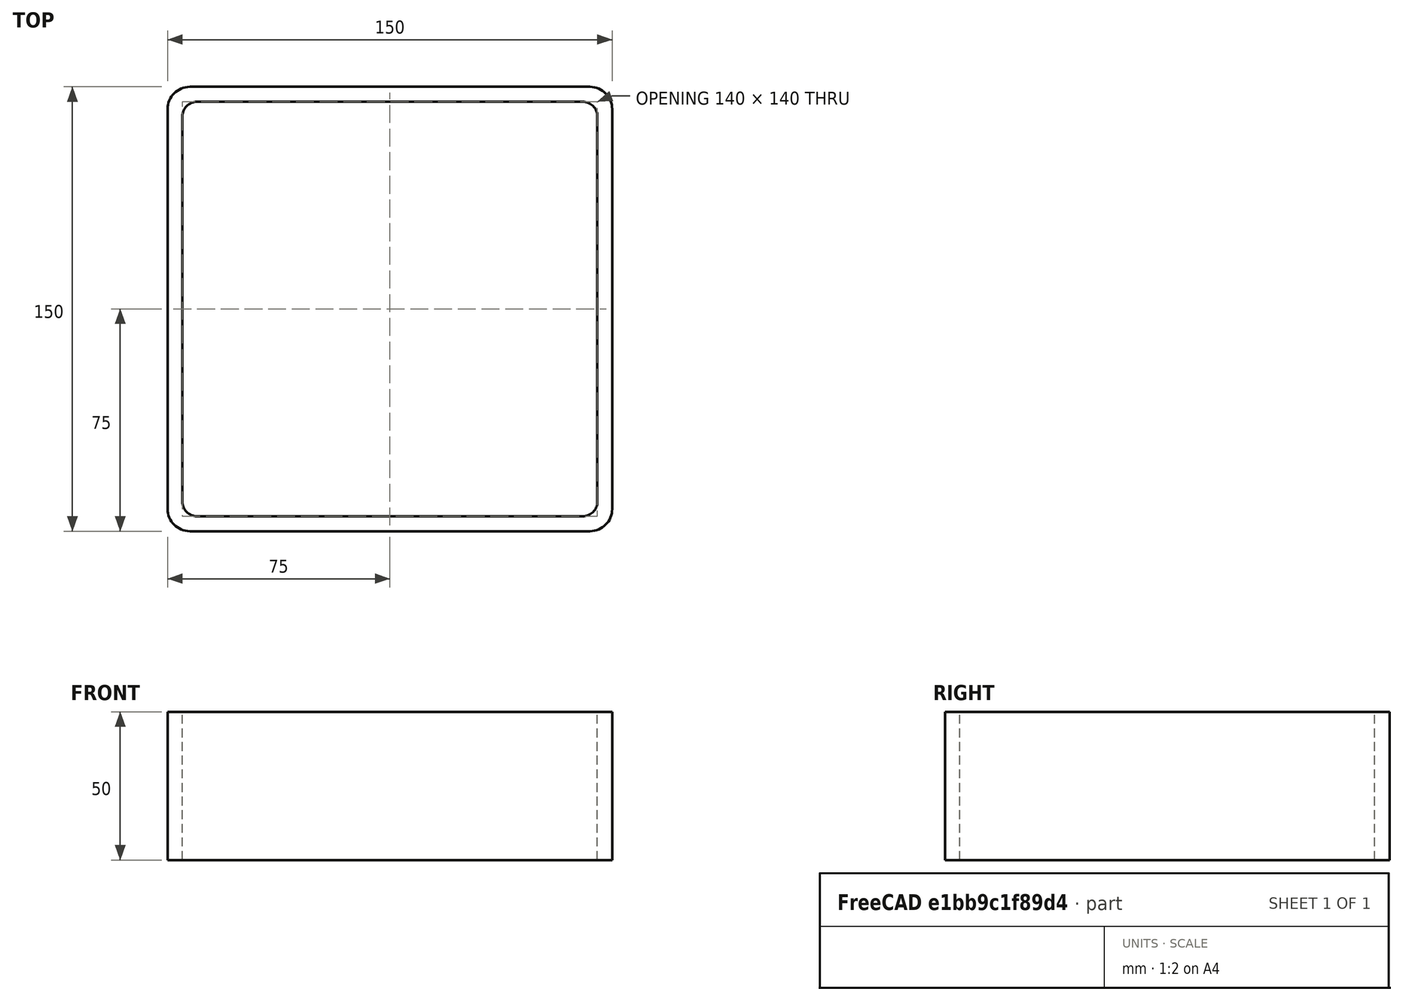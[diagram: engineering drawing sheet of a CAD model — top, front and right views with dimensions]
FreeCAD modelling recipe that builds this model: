
FCSTD DOCUMENT  (FreeCAD 0.15R4671 (Git))
Label: Square hollow section 150x150x5 EN10219 S235JRH
License: All rights reserved
LicenseURL: http://en.wikipedia.org/wiki/All_rights_reserved
objects: Sketcher::SketchObject×1, Part::Extrusion×1
note: 2 computed .brp shape members not serialized (recipe doc carries the construction recipe); baked Part::Feature solids carry a one-line shape summary decoded from their .brp

FEATURE [Sketcher::SketchObject] Sketch
  sketch-geometry (16):
    g0: LineSegment StartX=-65 StartY=70 StartZ=0 EndX=65 EndY=70 EndZ=0
    g1: LineSegment StartX=70 StartY=65 StartZ=0 EndX=70 EndY=-65 EndZ=0
    g2: LineSegment StartX=65 StartY=-70 StartZ=0 EndX=-65 EndY=-70 EndZ=0
    g3: LineSegment StartX=-70 StartY=-65 StartZ=0 EndX=-70 EndY=65 EndZ=0
    g4: LineSegment StartX=-67.5 StartY=75 StartZ=0 EndX=67.5 EndY=75 EndZ=0
    g5: LineSegment StartX=75 StartY=67.5 StartZ=0 EndX=75 EndY=-67.5 EndZ=0
    g6: LineSegment StartX=67.5 StartY=-75 StartZ=0 EndX=-67.5 EndY=-75 EndZ=0
    g7: LineSegment StartX=-75 StartY=-67.5 StartZ=0 EndX=-75 EndY=67.5 EndZ=0
    g8: ArcOfCircle CenterX=-65 CenterY=65 CenterZ=0 NormalX=0 NormalY=0 NormalZ=1 Radius=5 StartAngle=1.5708 EndAngle=3.14159
    g9: ArcOfCircle CenterX=65 CenterY=65 CenterZ=0 NormalX=0 NormalY=0 NormalZ=1 Radius=5 StartAngle=0 EndAngle=1.5708
    g10: ArcOfCircle CenterX=65 CenterY=-65 CenterZ=0 NormalX=0 NormalY=0 NormalZ=1 Radius=5 StartAngle=4.71239 EndAngle=6.28319
    g11: ArcOfCircle CenterX=-65 CenterY=-65 CenterZ=0 NormalX=0 NormalY=0 NormalZ=1 Radius=5 StartAngle=3.14159 EndAngle=4.71239
    g12: ArcOfCircle CenterX=67.5 CenterY=67.5 CenterZ=0 NormalX=0 NormalY=0 NormalZ=1 Radius=7.5 StartAngle=0 EndAngle=1.5708
    g13: ArcOfCircle CenterX=67.5 CenterY=-67.5 CenterZ=0 NormalX=0 NormalY=0 NormalZ=1 Radius=7.5 StartAngle=4.71239 EndAngle=6.28319
    g14: ArcOfCircle CenterX=-67.5 CenterY=-67.5 CenterZ=0 NormalX=0 NormalY=0 NormalZ=1 Radius=7.5 StartAngle=3.14159 EndAngle=4.71239
    g15: ArcOfCircle CenterX=-67.5 CenterY=67.5 CenterZ=0 NormalX=0 NormalY=0 NormalZ=1 Radius=7.5 StartAngle=1.5708 EndAngle=3.14159
  constraints (36):
    c: Horizontal(g2)
    c: Vertical(g3)
    c: Horizontal(g6)
    c: Vertical(g7)
    c: Tangent(g3,g8) = 1.5708
    c: Tangent(g0,g8) = 1.5708
    c: Tangent(g0,g9) = 1.5708
    c: Tangent(g1,g9) = 1.5708
    c: Tangent(g1,g10) = 1.5708
    c: Tangent(g2,g10) = 1.5708
    c: Tangent(g2,g11) = 1.5708
    c: Tangent(g3,g11) = 1.5708
    c: Tangent(g4,g12) = 1.5708
    c: Tangent(g5,g12) = 1.5708
    c: Tangent(g5,g13) = 1.5708
    c: Tangent(g6,g13) = 1.5708
    c: Tangent(g6,g14) = 1.5708
    c: Tangent(g7,g14) = 1.5708
    c: Tangent(g7,g15) = 1.5708
    c: Tangent(g4,g15) = 1.5708
    c: Equal(g9,g8)
    c: Equal(g9,g11)
    c: Equal(g9,g10)
    c: Equal(g12,g15)
    c: Equal(g12,g14)
    c: Equal(g12,g13)
    c: Symmetric(g4,g6,g-1)
    c: Symmetric(g7,g5,g-2)
    c: DistanceY(g4,g6) = -150
    c: DistanceX(g7,g5) = 150
    c: Symmetric(g3,g1,g-2)
    c: Symmetric(g0,g2,g-1)
    c: DistanceY(g0,g4) = 5
    c: DistanceX(g5,g1) = -5
    c: Radius(g9) = 5
    c: Radius(g12) = 7.5
FEATURE [Part::Extrusion] Extrude  label="Square hollow section 150x150x5 EN10219 S235JRH"
  Base = -> Sketch
  Dir = (0,0,50)
  Solid = true
